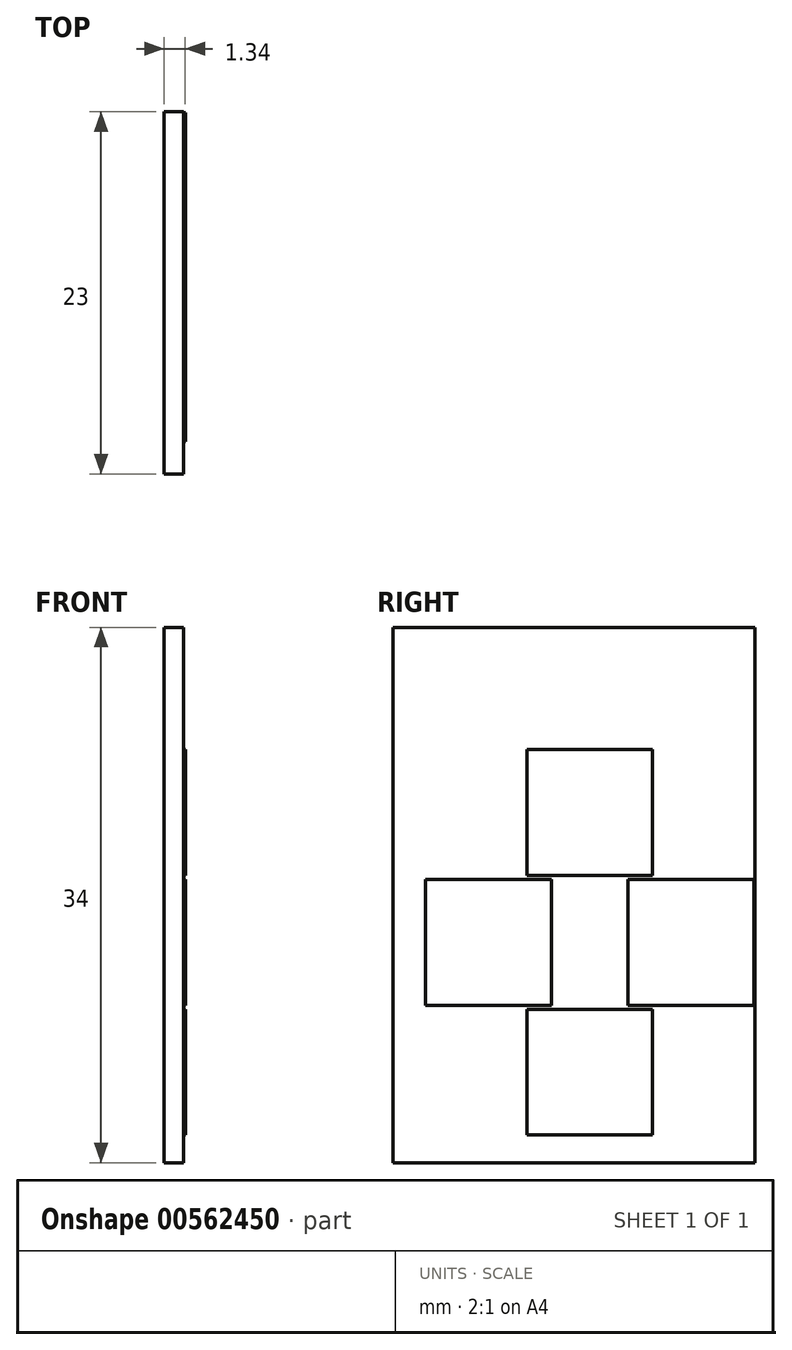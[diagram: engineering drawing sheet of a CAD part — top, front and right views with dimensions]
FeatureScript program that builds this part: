
annotation { "Feature Type Name" : "Feature", "Feature Type Description" : "" }
export const myFeature = defineFeature(function(context is Context, id is Id, definition is map)
    precondition{}
    {
        {
            var Q0;
            Q0=qCreatedBy(makeId("Right.planeOp"),FACE);
            var sketch = newSketch(context, id + "F0", { "sketchPlane" : qUnion([Q0])});
            skLineSegment(sketch, "E0.bottom", {"start": v(-11.5, 17) * mm, "end": v(11.5, 17) * mm});
            skLineSegment(sketch, "E0.top", {"start": v(-11.5, -17) * mm, "end": v(11.5, -17) * mm});
            skLineSegment(sketch, "E0.left", {"start": v(-11.5, 17) * mm, "end": v(-11.5, -17) * mm});
            skLineSegment(sketch, "E0.right", {"start": v(11.5, 17) * mm, "end": v(11.5, -17) * mm});
            skPoint(sketch, "E0.middle", {"position": v(0, 0) * mm});
            skSolve(sketch);
        }
        {
            var Q0;
            Q0=makeQuery(id+"F0.imprint","IMPRINT",FACE,{"disambiguationData":[TD([[makeQuery(id+"F0.imprint","IMPRINT",EDGE,{"derivedFrom":sQuery(id+"F0.wireOp",EDGE,"E0.bottom")}),-1.0]])]});
            extrude(context, id + "F1", {"entities" : qUnion([Q0]), "depth" : 1.25 * mm, "offsetDistance" : 25 * mm, "symmetric" : true});
        }
        {
            var Q0;
            Q0=makeQuery(id+"F1.opExtrude","CAP_FACE",FACE,{"disambiguationData":[OSD([sQuery(id+"F0.wireOp",EDGE,"E0.bottom"),sQuery(id+"F0.wireOp",EDGE,"E0.top"),sQuery(id+"F0.wireOp",EDGE,"E0.left"),sQuery(id+"F0.wireOp",EDGE,"E0.right")])],"isStart":false});
            var sketch = newSketch(context, id + "F2", { "sketchPlane" : qUnion([Q0])});
            skLineSegment(sketch, "E1.bottom", {"start": v(-2.38, 6.5) * mm, "end": v(4.37, 6.5) * mm, "construction": true});
            skLineSegment(sketch, "E1.top", {"start": v(-2.38, -12.5) * mm, "end": v(4.37, -12.5) * mm, "construction": true});
            skLineSegment(sketch, "E1.left", {"start": v(-2.38, 6.5) * mm, "end": v(-2.38, -12.5) * mm, "construction": true});
            skLineSegment(sketch, "E1.right", {"start": v(4.37, 6.5) * mm, "end": v(4.37, -12.5) * mm, "construction": true});
            skPoint(sketch, "E1.middle", {"position": v(1, -3) * mm});
            skLineSegment(sketch, "E2.bottom", {"start": v(-8.5, 0.37) * mm, "end": v(10.5, 0.37) * mm, "construction": true});
            skLineSegment(sketch, "E2.top", {"start": v(-8.5, -6.38) * mm, "end": v(10.5, -6.38) * mm, "construction": true});
            skLineSegment(sketch, "E2.left", {"start": v(-8.5, 0.37) * mm, "end": v(-8.5, -6.38) * mm, "construction": true});
            skLineSegment(sketch, "E2.right", {"start": v(10.5, 0.37) * mm, "end": v(10.5, -6.38) * mm, "construction": true});
            skLineSegment(sketch, "E3.bottom", {"start": v(-9.44, 1) * mm, "end": v(-1.44, 1) * mm});
            skLineSegment(sketch, "E3.top", {"start": v(-9.44, -7) * mm, "end": v(-1.44, -7) * mm});
            skLineSegment(sketch, "E3.left", {"start": v(-9.44, 1) * mm, "end": v(-9.44, -7) * mm});
            skLineSegment(sketch, "E3.right", {"start": v(-1.44, 1) * mm, "end": v(-1.44, -7) * mm});
            skPoint(sketch, "E3.middle", {"position": v(-5.44, -3) * mm});
            skPoint(sketch, "E3.middle.positionSnap0", {"position": v(-8.5, -3) * mm});
            skPoint(sketch, "E3.centerSnap0", {"position": v(-8.5, -3) * mm});
            skLineSegment(sketch, "E4.bottom", {"start": v(3.44, 1) * mm, "end": v(11.44, 1) * mm});
            skLineSegment(sketch, "E4.top", {"start": v(3.44, -7) * mm, "end": v(11.44, -7) * mm});
            skLineSegment(sketch, "E4.left", {"start": v(3.44, 1) * mm, "end": v(3.44, -7) * mm});
            skLineSegment(sketch, "E4.right", {"start": v(11.44, 1) * mm, "end": v(11.44, -7) * mm});
            skPoint(sketch, "E4.middle", {"position": v(7.44, -3) * mm});
            skPoint(sketch, "E4.middle.positionSnap0", {"position": v(10.5, -3) * mm});
            skPoint(sketch, "E4.centerSnap0", {"position": v(10.5, -3) * mm});
            skLineSegment(sketch, "E5.bottom", {"start": v(-3, 9.25) * mm, "end": v(5, 9.25) * mm});
            skLineSegment(sketch, "E5.top", {"start": v(-3, 1.25) * mm, "end": v(5, 1.25) * mm});
            skLineSegment(sketch, "E5.left", {"start": v(-3, 9.25) * mm, "end": v(-3, 1.25) * mm});
            skLineSegment(sketch, "E5.right", {"start": v(5, 9.25) * mm, "end": v(5, 1.25) * mm});
            skPoint(sketch, "E5.middle", {"position": v(1, 5.25) * mm});
            skPoint(sketch, "E5.middle.positionSnap0", {"position": v(1, 6.5) * mm});
            skPoint(sketch, "E5.centerSnap0", {"position": v(1, 6.5) * mm});
            skLineSegment(sketch, "E6.bottom", {"start": v(-3, -7.25) * mm, "end": v(5, -7.25) * mm});
            skLineSegment(sketch, "E6.top", {"start": v(-3, -15.25) * mm, "end": v(5, -15.25) * mm});
            skLineSegment(sketch, "E6.left", {"start": v(-3, -7.25) * mm, "end": v(-3, -15.25) * mm});
            skLineSegment(sketch, "E6.right", {"start": v(5, -7.25) * mm, "end": v(5, -15.25) * mm});
            skPoint(sketch, "E6.middle", {"position": v(1, -11.25) * mm});
            skPoint(sketch, "E6.middle.positionSnap0", {"position": v(1, -12.5) * mm});
            skPoint(sketch, "E6.centerSnap0", {"position": v(1, -12.5) * mm});
            skSolve(sketch);
        }
        {
            var Q0;
            Q0 = qSketchRegion(id + "F2", true);
            extrude(context, id + "F3", {"entities" : qUnion([Q0]), "operationType" : NewBodyOperationType.ADD, "depth" : .1 * mm, "offsetDistance" : 25 * mm});
        }
    });
